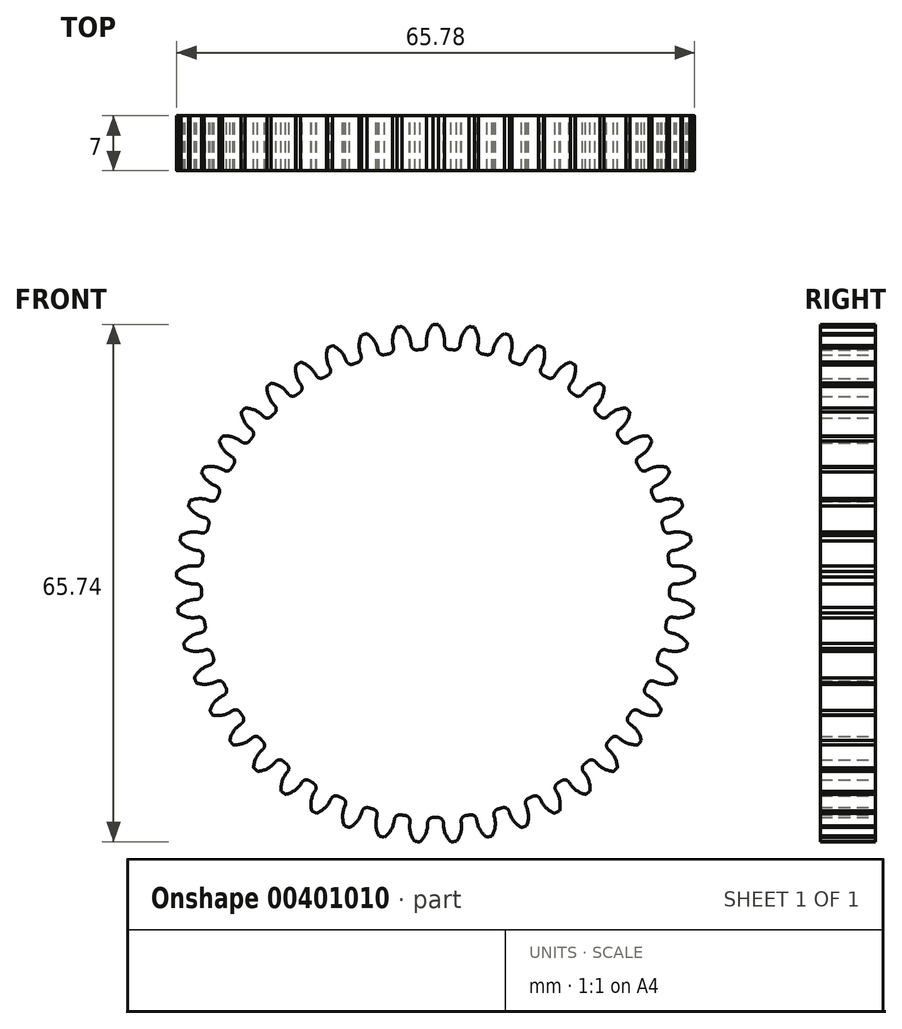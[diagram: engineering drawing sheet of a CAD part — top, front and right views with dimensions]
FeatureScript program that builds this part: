
annotation { "Feature Type Name" : "Feature", "Feature Type Description" : "" }
export const myFeature = defineFeature(function(context is Context, id is Id, definition is map)
    precondition{}
    {
        {
            var Q0;
            Q0=qCreatedBy(makeId("Front.planeOp"),FACE);
            var sketch = newSketch(context, id + "F0", { "sketchPlane" : qUnion([Q0])});
            skArc(sketch, "E0.0.0", {"start": v(-1.8, 30.22) * mm, "mid": v(-2.09, 30.2) * mm, "end": v(-2.38, 30.18) * mm});
            skArc(sketch, "E0.0.1", {"start": v(-2.38, 30.18) * mm, "mid": v(-2.9, 30.36) * mm, "end": v(-3.14, 30.85) * mm});
            skArc(sketch, "E0.0.2", {"start": v(-3.14, 30.85) * mm, "mid": v(-3.45, 32.12) * mm, "end": v(-4.25, 33.15) * mm});
            skArc(sketch, "E0.0.3", {"start": v(-4.25, 33.15) * mm, "mid": v(-4.6, 33.1) * mm, "end": v(-4.93, 33.06) * mm});
            skArc(sketch, "E0.0.4", {"start": v(-4.93, 33.06) * mm, "mid": v(-5.42, 31.84) * mm, "end": v(-5.37, 30.54) * mm});
            skArc(sketch, "E0.0.5", {"start": v(-5.37, 30.54) * mm, "mid": v(-5.46, 30) * mm, "end": v(-5.91, 29.69) * mm});
            skArc(sketch, "E0.0.6", {"start": v(-5.91, 29.69) * mm, "mid": v(-6.2, 29.63) * mm, "end": v(-6.49, 29.56) * mm});
            skArc(sketch, "E0.0.7", {"start": v(-6.49, 29.56) * mm, "mid": v(-7.03, 29.67) * mm, "end": v(-7.33, 30.12) * mm});
            skArc(sketch, "E0.0.8", {"start": v(-7.33, 30.12) * mm, "mid": v(-7.82, 31.33) * mm, "end": v(-8.75, 32.25) * mm});
            skArc(sketch, "E0.0.9", {"start": v(-8.75, 32.25) * mm, "mid": v(-9.08, 32.15) * mm, "end": v(-9.41, 32.06) * mm});
            skArc(sketch, "E0.0.10", {"start": v(-9.41, 32.06) * mm, "mid": v(-9.72, 30.79) * mm, "end": v(-9.5, 29.5) * mm});
            skArc(sketch, "E0.0.11", {"start": v(-9.5, 29.5) * mm, "mid": v(-9.5, 28.95) * mm, "end": v(-9.91, 28.58) * mm});
            skArc(sketch, "E0.0.12", {"start": v(-9.91, 28.58) * mm, "mid": v(-10.19, 28.48) * mm, "end": v(-10.46, 28.38) * mm});
            skArc(sketch, "E0.0.13", {"start": v(-10.46, 28.38) * mm, "mid": v(-11.01, 28.4) * mm, "end": v(-11.38, 28.82) * mm});
            skArc(sketch, "E0.0.14", {"start": v(-11.38, 28.82) * mm, "mid": v(-12.03, 29.95) * mm, "end": v(-13.08, 30.72) * mm});
            skArc(sketch, "E0.0.15", {"start": v(-13.08, 30.72) * mm, "mid": v(-13.4, 30.58) * mm, "end": v(-13.7, 30.44) * mm});
            skArc(sketch, "E0.0.16", {"start": v(-13.7, 30.44) * mm, "mid": v(-13.84, 29.14) * mm, "end": v(-13.44, 27.9) * mm});
            skArc(sketch, "E0.0.17", {"start": v(-13.44, 27.9) * mm, "mid": v(-13.37, 27.36) * mm, "end": v(-13.72, 26.93) * mm});
            skArc(sketch, "E0.0.18", {"start": v(-13.72, 26.93) * mm, "mid": v(-13.98, 26.8) * mm, "end": v(-14.24, 26.66) * mm});
            skArc(sketch, "E0.0.19", {"start": v(-14.24, 26.66) * mm, "mid": v(-14.79, 26.6) * mm, "end": v(-15.2, 26.96) * mm});
            skArc(sketch, "E0.0.20", {"start": v(-15.2, 26.96) * mm, "mid": v(-16, 28) * mm, "end": v(-17.15, 28.6) * mm});
            skArc(sketch, "E0.0.21", {"start": v(-17.15, 28.6) * mm, "mid": v(-17.45, 28.43) * mm, "end": v(-17.74, 28.24) * mm});
            skArc(sketch, "E0.0.22", {"start": v(-17.74, 28.24) * mm, "mid": v(-17.69, 26.94) * mm, "end": v(-17.11, 25.77) * mm});
            skArc(sketch, "E0.0.23", {"start": v(-17.11, 25.77) * mm, "mid": v(-16.97, 25.24) * mm, "end": v(-17.26, 24.77) * mm});
            skArc(sketch, "E0.0.24", {"start": v(-17.26, 24.77) * mm, "mid": v(-17.5, 24.6) * mm, "end": v(-17.74, 24.42) * mm});
            skArc(sketch, "E0.0.25", {"start": v(-17.74, 24.42) * mm, "mid": v(-18.27, 24.3) * mm, "end": v(-18.73, 24.6) * mm});
            skArc(sketch, "E0.0.26", {"start": v(-18.73, 24.6) * mm, "mid": v(-19.67, 25.5) * mm, "end": v(-20.9, 25.95) * mm});
            skArc(sketch, "E0.0.27", {"start": v(-20.9, 25.95) * mm, "mid": v(-21.16, 25.73) * mm, "end": v(-21.42, 25.5) * mm});
            skArc(sketch, "E0.0.28", {"start": v(-21.42, 25.5) * mm, "mid": v(-21.2, 24.22) * mm, "end": v(-20.46, 23.14) * mm});
            skArc(sketch, "E0.0.29", {"start": v(-20.46, 23.14) * mm, "mid": v(-20.25, 22.63) * mm, "end": v(-20.47, 22.13) * mm});
            skArc(sketch, "E0.0.30", {"start": v(-20.47, 22.13) * mm, "mid": v(-20.68, 21.93) * mm, "end": v(-20.89, 21.72) * mm});
            skArc(sketch, "E0.0.31", {"start": v(-20.89, 21.72) * mm, "mid": v(-21.4, 21.52) * mm, "end": v(-21.9, 21.75) * mm});
            skArc(sketch, "E0.0.32", {"start": v(-21.9, 21.75) * mm, "mid": v(-22.96, 22.52) * mm, "end": v(-24.23, 22.8) * mm});
            skArc(sketch, "E0.0.33", {"start": v(-24.23, 22.8) * mm, "mid": v(-24.46, 22.54) * mm, "end": v(-24.7, 22.28) * mm});
            skArc(sketch, "E0.0.34", {"start": v(-24.7, 22.28) * mm, "mid": v(-24.28, 21.05) * mm, "end": v(-23.4, 20.08) * mm});
            skArc(sketch, "E0.0.35", {"start": v(-23.4, 20.08) * mm, "mid": v(-23.13, 19.6) * mm, "end": v(-23.27, 19.07) * mm});
            skArc(sketch, "E0.0.36", {"start": v(-23.27, 19.07) * mm, "mid": v(-23.46, 18.84) * mm, "end": v(-23.64, 18.61) * mm});
            skArc(sketch, "E0.0.37", {"start": v(-23.64, 18.61) * mm, "mid": v(-24.11, 18.34) * mm, "end": v(-24.64, 18.5) * mm});
            skArc(sketch, "E0.0.38", {"start": v(-24.64, 18.5) * mm, "mid": v(-25.8, 19.11) * mm, "end": v(-27.1, 19.2) * mm});
            skArc(sketch, "E0.0.39", {"start": v(-27.1, 19.2) * mm, "mid": v(-27.29, 18.92) * mm, "end": v(-27.48, 18.64) * mm});
            skArc(sketch, "E0.0.40", {"start": v(-27.48, 18.64) * mm, "mid": v(-26.9, 17.47) * mm, "end": v(-25.9, 16.63) * mm});
            skArc(sketch, "E0.0.41", {"start": v(-25.9, 16.63) * mm, "mid": v(-25.56, 16.2) * mm, "end": v(-25.63, 15.66) * mm});
            skArc(sketch, "E0.0.42", {"start": v(-25.63, 15.66) * mm, "mid": v(-25.78, 15.4) * mm, "end": v(-25.92, 15.15) * mm});
            skArc(sketch, "E0.0.43", {"start": v(-25.92, 15.15) * mm, "mid": v(-26.36, 14.81) * mm, "end": v(-26.9, 14.9) * mm});
            skArc(sketch, "E0.0.44", {"start": v(-26.9, 14.9) * mm, "mid": v(-28.13, 15.34) * mm, "end": v(-29.43, 15.26) * mm});
            skArc(sketch, "E0.0.45", {"start": v(-29.43, 15.26) * mm, "mid": v(-29.58, 14.95) * mm, "end": v(-29.73, 14.64) * mm});
            skArc(sketch, "E0.0.46", {"start": v(-29.73, 14.64) * mm, "mid": v(-29, 13.56) * mm, "end": v(-27.9, 12.87) * mm});
            skArc(sketch, "E0.0.47", {"start": v(-27.9, 12.87) * mm, "mid": v(-27.5, 12.5) * mm, "end": v(-27.49, 11.94) * mm});
            skArc(sketch, "E0.0.48", {"start": v(-27.49, 11.94) * mm, "mid": v(-27.6, 11.67) * mm, "end": v(-27.7, 11.4) * mm});
            skArc(sketch, "E0.0.49", {"start": v(-27.7, 11.4) * mm, "mid": v(-28.1, 11) * mm, "end": v(-28.64, 11.01) * mm});
            skArc(sketch, "E0.0.50", {"start": v(-28.64, 11.01) * mm, "mid": v(-29.92, 11.29) * mm, "end": v(-31.2, 11.02) * mm});
            skArc(sketch, "E0.0.51", {"start": v(-31.2, 11.02) * mm, "mid": v(-31.3, 10.7) * mm, "end": v(-31.4, 10.37) * mm});
            skArc(sketch, "E0.0.52", {"start": v(-31.4, 10.37) * mm, "mid": v(-30.53, 9.4) * mm, "end": v(-29.34, 8.87) * mm});
            skArc(sketch, "E0.0.53", {"start": v(-29.34, 8.87) * mm, "mid": v(-28.89, 8.55) * mm, "end": v(-28.8, 8) * mm});
            skArc(sketch, "E0.0.54", {"start": v(-28.8, 8) * mm, "mid": v(-28.88, 7.72) * mm, "end": v(-28.95, 7.44) * mm});
            skArc(sketch, "E0.0.55", {"start": v(-28.95, 7.44) * mm, "mid": v(-29.28, 7) * mm, "end": v(-29.82, 6.93) * mm});
            skArc(sketch, "E0.0.56", {"start": v(-29.82, 6.93) * mm, "mid": v(-31.12, 7.02) * mm, "end": v(-32.35, 6.58) * mm});
            skArc(sketch, "E0.0.57", {"start": v(-32.35, 6.58) * mm, "mid": v(-32.41, 6.24) * mm, "end": v(-32.47, 5.9) * mm});
            skArc(sketch, "E0.0.58", {"start": v(-32.47, 5.9) * mm, "mid": v(-31.47, 5.07) * mm, "end": v(-30.21, 4.7) * mm});
            skArc(sketch, "E0.0.59", {"start": v(-30.21, 4.7) * mm, "mid": v(-29.72, 4.46) * mm, "end": v(-29.57, 3.93) * mm});
            skArc(sketch, "E0.0.60", {"start": v(-29.57, 3.93) * mm, "mid": v(-29.6, 3.64) * mm, "end": v(-29.63, 3.34) * mm});
            skArc(sketch, "E0.0.61", {"start": v(-29.63, 3.34) * mm, "mid": v(-29.9, 2.86) * mm, "end": v(-30.42, 2.72) * mm});
            skArc(sketch, "E0.0.62", {"start": v(-30.42, 2.72) * mm, "mid": v(-31.72, 2.63) * mm, "end": v(-32.88, 2.02) * mm});
            skArc(sketch, "E0.0.63", {"start": v(-32.88, 2.02) * mm, "mid": v(-32.9, 1.68) * mm, "end": v(-32.9, 1.33) * mm});
            skArc(sketch, "E0.0.64", {"start": v(-32.9, 1.33) * mm, "mid": v(-31.8, 0.65) * mm, "end": v(-30.5, 0.46) * mm});
            skArc(sketch, "E0.0.65", {"start": v(-30.5, 0.46) * mm, "mid": v(-29.98, 0.28) * mm, "end": v(-29.75, -0.22) * mm});
            skArc(sketch, "E0.0.66", {"start": v(-29.75, -0.22) * mm, "mid": v(-29.75, -0.51) * mm, "end": v(-29.73, -0.8) * mm});
            skArc(sketch, "E0.0.67", {"start": v(-29.73, -0.8) * mm, "mid": v(-29.93, -1.32) * mm, "end": v(-30.43, -1.54) * mm});
            skArc(sketch, "E0.0.68", {"start": v(-30.43, -1.54) * mm, "mid": v(-31.7, -1.8) * mm, "end": v(-32.77, -2.57) * mm});
            skArc(sketch, "E0.0.69", {"start": v(-32.77, -2.57) * mm, "mid": v(-32.73, -2.91) * mm, "end": v(-32.7, -3.25) * mm});
            skArc(sketch, "E0.0.70", {"start": v(-32.7, -3.25) * mm, "mid": v(-31.5, -3.78) * mm, "end": v(-30.2, -3.78) * mm});
            skArc(sketch, "E0.0.71", {"start": v(-30.2, -3.78) * mm, "mid": v(-29.66, -3.89) * mm, "end": v(-29.36, -4.35) * mm});
            skArc(sketch, "E0.0.72", {"start": v(-29.36, -4.35) * mm, "mid": v(-29.31, -4.64) * mm, "end": v(-29.26, -4.93) * mm});
            skArc(sketch, "E0.0.73", {"start": v(-29.26, -4.93) * mm, "mid": v(-29.38, -5.46) * mm, "end": v(-29.85, -5.75) * mm});
            skArc(sketch, "E0.0.74", {"start": v(-29.85, -5.75) * mm, "mid": v(-31.07, -6.2) * mm, "end": v(-32.02, -7.1) * mm});
            skArc(sketch, "E0.0.75", {"start": v(-32.02, -7.1) * mm, "mid": v(-31.94, -7.43) * mm, "end": v(-31.85, -7.77) * mm});
            skArc(sketch, "E0.0.76", {"start": v(-31.85, -7.77) * mm, "mid": v(-30.6, -8.12) * mm, "end": v(-29.3, -7.94) * mm});
            skArc(sketch, "E0.0.77", {"start": v(-29.3, -7.94) * mm, "mid": v(-28.75, -7.97) * mm, "end": v(-28.4, -8.39) * mm});
            skArc(sketch, "E0.0.78", {"start": v(-28.4, -8.39) * mm, "mid": v(-28.3, -8.67) * mm, "end": v(-28.22, -8.95) * mm});
            skArc(sketch, "E0.0.79", {"start": v(-28.22, -8.95) * mm, "mid": v(-28.26, -9.5) * mm, "end": v(-28.68, -9.84) * mm});
            skArc(sketch, "E0.0.80", {"start": v(-28.68, -9.84) * mm, "mid": v(-29.84, -10.45) * mm, "end": v(-30.65, -11.48) * mm});
            skArc(sketch, "E0.0.81", {"start": v(-30.65, -11.48) * mm, "mid": v(-30.52, -11.8) * mm, "end": v(-30.39, -12.12) * mm});
            skArc(sketch, "E0.0.82", {"start": v(-30.39, -12.12) * mm, "mid": v(-29.1, -12.3) * mm, "end": v(-27.84, -11.93) * mm});
            skArc(sketch, "E0.0.83", {"start": v(-27.84, -11.93) * mm, "mid": v(-27.3, -11.89) * mm, "end": v(-26.88, -12.25) * mm});
            skArc(sketch, "E0.0.84", {"start": v(-26.88, -12.25) * mm, "mid": v(-26.75, -12.51) * mm, "end": v(-26.62, -12.78) * mm});
            skArc(sketch, "E0.0.85", {"start": v(-26.62, -12.78) * mm, "mid": v(-26.59, -13.33) * mm, "end": v(-26.96, -13.73) * mm});
            skArc(sketch, "E0.0.86", {"start": v(-26.96, -13.73) * mm, "mid": v(-28.02, -14.5) * mm, "end": v(-28.68, -15.62) * mm});
            skArc(sketch, "E0.0.87", {"start": v(-28.68, -15.62) * mm, "mid": v(-28.5, -15.92) * mm, "end": v(-28.33, -16.22) * mm});
            skArc(sketch, "E0.0.88", {"start": v(-28.33, -16.22) * mm, "mid": v(-27.03, -16.21) * mm, "end": v(-25.83, -15.68) * mm});
            skArc(sketch, "E0.0.89", {"start": v(-25.83, -15.68) * mm, "mid": v(-25.3, -15.56) * mm, "end": v(-24.84, -15.86) * mm});
            skArc(sketch, "E0.0.90", {"start": v(-24.84, -15.86) * mm, "mid": v(-24.68, -16.1) * mm, "end": v(-24.51, -16.35) * mm});
            skArc(sketch, "E0.0.91", {"start": v(-24.51, -16.35) * mm, "mid": v(-24.4, -16.9) * mm, "end": v(-24.72, -17.34) * mm});
            skArc(sketch, "E0.0.92", {"start": v(-24.72, -17.34) * mm, "mid": v(-25.65, -18.25) * mm, "end": v(-26.15, -19.46) * mm});
            skArc(sketch, "E0.0.93", {"start": v(-26.15, -19.46) * mm, "mid": v(-25.94, -19.73) * mm, "end": v(-25.73, -20) * mm});
            skArc(sketch, "E0.0.94", {"start": v(-25.73, -20) * mm, "mid": v(-24.43, -19.81) * mm, "end": v(-23.33, -19.12) * mm});
            skArc(sketch, "E0.0.95", {"start": v(-23.33, -19.12) * mm, "mid": v(-22.81, -18.92) * mm, "end": v(-22.32, -19.16) * mm});
            skArc(sketch, "E0.0.96", {"start": v(-22.32, -19.16) * mm, "mid": v(-22.12, -19.38) * mm, "end": v(-21.92, -19.6) * mm});
            skArc(sketch, "E0.0.97", {"start": v(-21.92, -19.6) * mm, "mid": v(-21.74, -20.12) * mm, "end": v(-21.99, -20.6) * mm});
            skArc(sketch, "E0.0.98", {"start": v(-21.99, -20.6) * mm, "mid": v(-22.8, -21.63) * mm, "end": v(-23.11, -22.9) * mm});
            skArc(sketch, "E0.0.99", {"start": v(-23.11, -22.9) * mm, "mid": v(-22.87, -23.14) * mm, "end": v(-22.62, -23.38) * mm});
            skArc(sketch, "E0.0.100", {"start": v(-22.62, -23.38) * mm, "mid": v(-21.37, -23.01) * mm, "end": v(-20.37, -22.17) * mm});
            skArc(sketch, "E0.0.101", {"start": v(-20.37, -22.17) * mm, "mid": v(-19.88, -21.9) * mm, "end": v(-19.36, -22.07) * mm});
            skArc(sketch, "E0.0.102", {"start": v(-19.36, -22.07) * mm, "mid": v(-19.14, -22.26) * mm, "end": v(-18.91, -22.45) * mm});
            skArc(sketch, "E0.0.103", {"start": v(-18.91, -22.45) * mm, "mid": v(-18.66, -22.94) * mm, "end": v(-18.83, -23.46) * mm});
            skArc(sketch, "E0.0.104", {"start": v(-18.83, -23.46) * mm, "mid": v(-19.49, -24.59) * mm, "end": v(-19.63, -25.89) * mm});
            skArc(sketch, "E0.0.105", {"start": v(-19.63, -25.89) * mm, "mid": v(-19.35, -26.09) * mm, "end": v(-19.07, -26.3) * mm});
            skArc(sketch, "E0.0.106", {"start": v(-19.07, -26.3) * mm, "mid": v(-17.88, -25.75) * mm, "end": v(-17, -24.78) * mm});
            skArc(sketch, "E0.0.107", {"start": v(-17, -24.78) * mm, "mid": v(-16.57, -24.45) * mm, "end": v(-16.03, -24.55) * mm});
            skArc(sketch, "E0.0.108", {"start": v(-16.03, -24.55) * mm, "mid": v(-15.78, -24.7) * mm, "end": v(-15.53, -24.86) * mm});
            skArc(sketch, "E0.0.109", {"start": v(-15.53, -24.86) * mm, "mid": v(-15.2, -25.3) * mm, "end": v(-15.31, -25.84) * mm});
            skArc(sketch, "E0.0.110", {"start": v(-15.31, -25.84) * mm, "mid": v(-15.8, -27.05) * mm, "end": v(-15.76, -28.36) * mm});
            skArc(sketch, "E0.0.111", {"start": v(-15.76, -28.36) * mm, "mid": v(-15.46, -28.52) * mm, "end": v(-15.15, -28.68) * mm});
            skArc(sketch, "E0.0.112", {"start": v(-15.15, -28.68) * mm, "mid": v(-14.05, -27.98) * mm, "end": v(-13.32, -26.9) * mm});
            skArc(sketch, "E0.0.113", {"start": v(-13.32, -26.9) * mm, "mid": v(-12.93, -26.52) * mm, "end": v(-12.38, -26.53) * mm});
            skArc(sketch, "E0.0.114", {"start": v(-12.38, -26.53) * mm, "mid": v(-12.11, -26.65) * mm, "end": v(-11.84, -26.77) * mm});
            skArc(sketch, "E0.0.115", {"start": v(-11.84, -26.77) * mm, "mid": v(-11.47, -27.17) * mm, "end": v(-11.5, -27.72) * mm});
            skArc(sketch, "E0.0.116", {"start": v(-11.5, -27.72) * mm, "mid": v(-11.8, -28.98) * mm, "end": v(-11.59, -30.27) * mm});
            skArc(sketch, "E0.0.117", {"start": v(-11.59, -30.27) * mm, "mid": v(-11.27, -30.39) * mm, "end": v(-10.94, -30.5) * mm});
            skArc(sketch, "E0.0.118", {"start": v(-10.94, -30.5) * mm, "mid": v(-9.95, -29.66) * mm, "end": v(-9.37, -28.49) * mm});
            skArc(sketch, "E0.0.119", {"start": v(-9.37, -28.49) * mm, "mid": v(-9.04, -28.05) * mm, "end": v(-8.5, -27.99) * mm});
            skArc(sketch, "E0.0.120", {"start": v(-8.5, -27.99) * mm, "mid": v(-8.21, -28.07) * mm, "end": v(-7.93, -28.15) * mm});
            skArc(sketch, "E0.0.121", {"start": v(-7.93, -28.15) * mm, "mid": v(-7.5, -28.5) * mm, "end": v(-7.45, -29.04) * mm});
            skArc(sketch, "E0.0.122", {"start": v(-7.45, -29.04) * mm, "mid": v(-7.59, -30.34) * mm, "end": v(-7.2, -31.58) * mm});
            skArc(sketch, "E0.0.123", {"start": v(-7.2, -31.58) * mm, "mid": v(-6.85, -31.65) * mm, "end": v(-6.52, -31.72) * mm});
            skArc(sketch, "E0.0.124", {"start": v(-6.52, -31.72) * mm, "mid": v(-5.65, -30.75) * mm, "end": v(-5.24, -29.5) * mm});
            skArc(sketch, "E0.0.125", {"start": v(-5.24, -29.5) * mm, "mid": v(-4.98, -29.03) * mm, "end": v(-4.44, -28.9) * mm});
            skArc(sketch, "E0.0.126", {"start": v(-4.44, -28.9) * mm, "mid": v(-4.15, -28.93) * mm, "end": v(-3.86, -28.97) * mm});
            skArc(sketch, "E0.0.127", {"start": v(-3.86, -28.97) * mm, "mid": v(-3.39, -29.25) * mm, "end": v(-3.26, -29.79) * mm});
            skArc(sketch, "E0.0.128", {"start": v(-3.26, -29.79) * mm, "mid": v(-3.22, -31.1) * mm, "end": v(-2.65, -32.27) * mm});
            skArc(sketch, "E0.0.129", {"start": v(-2.65, -32.27) * mm, "mid": v(-2.3, -32.3) * mm, "end": v(-1.96, -32.31) * mm});
            skArc(sketch, "E0.0.130", {"start": v(-1.96, -32.31) * mm, "mid": v(-1.24, -31.23) * mm, "end": v(-1.01, -29.94) * mm});
            skArc(sketch, "E0.0.131", {"start": v(-1.01, -29.94) * mm, "mid": v(-0.81, -29.43) * mm, "end": v(-0.3, -29.22) * mm});
            skArc(sketch, "E0.0.132", {"start": v(-0.3, -29.22) * mm, "mid": v(-0.01, -29.22) * mm, "end": v(0.28, -29.22) * mm});
            skArc(sketch, "E0.0.133", {"start": v(0.28, -29.22) * mm, "mid": v(0.79, -29.43) * mm, "end": v(0.99, -29.94) * mm});
            skArc(sketch, "E0.0.134", {"start": v(0.99, -29.94) * mm, "mid": v(1.21, -31.23) * mm, "end": v(1.94, -32.31) * mm});
            skArc(sketch, "E0.0.135", {"start": v(1.94, -32.31) * mm, "mid": v(2.28, -32.3) * mm, "end": v(2.63, -32.27) * mm});
            skArc(sketch, "E0.0.136", {"start": v(2.63, -32.27) * mm, "mid": v(3.2, -31.1) * mm, "end": v(3.24, -29.79) * mm});
            skArc(sketch, "E0.0.137", {"start": v(3.24, -29.79) * mm, "mid": v(3.36, -29.25) * mm, "end": v(3.84, -28.97) * mm});
            skArc(sketch, "E0.0.138", {"start": v(3.84, -28.97) * mm, "mid": v(4.13, -28.93) * mm, "end": v(4.42, -28.9) * mm});
            skArc(sketch, "E0.0.139", {"start": v(4.42, -28.9) * mm, "mid": v(4.95, -29.03) * mm, "end": v(5.22, -29.5) * mm});
            skArc(sketch, "E0.0.140", {"start": v(5.22, -29.5) * mm, "mid": v(5.62, -30.75) * mm, "end": v(6.49, -31.72) * mm});
            skArc(sketch, "E0.0.141", {"start": v(6.49, -31.72) * mm, "mid": v(6.83, -31.65) * mm, "end": v(7.16, -31.58) * mm});
            skArc(sketch, "E0.0.142", {"start": v(7.16, -31.58) * mm, "mid": v(7.56, -30.34) * mm, "end": v(7.42, -29.04) * mm});
            skArc(sketch, "E0.0.143", {"start": v(7.42, -29.04) * mm, "mid": v(7.47, -28.5) * mm, "end": v(7.9, -28.15) * mm});
            skArc(sketch, "E0.0.144", {"start": v(7.9, -28.15) * mm, "mid": v(8.19, -28.07) * mm, "end": v(8.47, -27.99) * mm});
            skArc(sketch, "E0.0.145", {"start": v(8.47, -27.99) * mm, "mid": v(9.01, -28.05) * mm, "end": v(9.35, -28.49) * mm});
            skArc(sketch, "E0.0.146", {"start": v(9.35, -28.49) * mm, "mid": v(9.92, -29.66) * mm, "end": v(10.91, -30.5) * mm});
            skArc(sketch, "E0.0.147", {"start": v(10.91, -30.5) * mm, "mid": v(11.24, -30.39) * mm, "end": v(11.56, -30.27) * mm});
            skArc(sketch, "E0.0.148", {"start": v(11.56, -30.27) * mm, "mid": v(11.78, -28.98) * mm, "end": v(11.47, -27.72) * mm});
            skArc(sketch, "E0.0.149", {"start": v(11.47, -27.72) * mm, "mid": v(11.44, -27.17) * mm, "end": v(11.82, -26.77) * mm});
            skArc(sketch, "E0.0.150", {"start": v(11.82, -26.77) * mm, "mid": v(12.09, -26.65) * mm, "end": v(12.36, -26.53) * mm});
            skArc(sketch, "E0.0.151", {"start": v(12.36, -26.53) * mm, "mid": v(12.9, -26.52) * mm, "end": v(13.3, -26.9) * mm});
            skArc(sketch, "E0.0.152", {"start": v(13.3, -26.9) * mm, "mid": v(14.02, -27.98) * mm, "end": v(15.13, -28.68) * mm});
            skArc(sketch, "E0.0.153", {"start": v(15.13, -28.68) * mm, "mid": v(15.43, -28.52) * mm, "end": v(15.74, -28.36) * mm});
            skArc(sketch, "E0.0.154", {"start": v(15.74, -28.36) * mm, "mid": v(15.77, -27.05) * mm, "end": v(15.29, -25.84) * mm});
            skArc(sketch, "E0.0.155", {"start": v(15.29, -25.84) * mm, "mid": v(15.18, -25.3) * mm, "end": v(15.5, -24.86) * mm});
            skArc(sketch, "E0.0.156", {"start": v(15.5, -24.86) * mm, "mid": v(15.75, -24.7) * mm, "end": v(16, -24.55) * mm});
            skArc(sketch, "E0.0.157", {"start": v(16, -24.55) * mm, "mid": v(16.54, -24.45) * mm, "end": v(16.98, -24.78) * mm});
            skArc(sketch, "E0.0.158", {"start": v(16.98, -24.78) * mm, "mid": v(17.86, -25.75) * mm, "end": v(19.04, -26.3) * mm});
            skArc(sketch, "E0.0.159", {"start": v(19.04, -26.3) * mm, "mid": v(19.32, -26.09) * mm, "end": v(19.6, -25.89) * mm});
            skArc(sketch, "E0.0.160", {"start": v(19.6, -25.89) * mm, "mid": v(19.46, -24.59) * mm, "end": v(18.8, -23.46) * mm});
            skArc(sketch, "E0.0.161", {"start": v(18.8, -23.46) * mm, "mid": v(18.63, -22.94) * mm, "end": v(18.88, -22.45) * mm});
            skArc(sketch, "E0.0.162", {"start": v(18.88, -22.45) * mm, "mid": v(19.1, -22.26) * mm, "end": v(19.33, -22.07) * mm});
            skArc(sketch, "E0.0.163", {"start": v(19.33, -22.07) * mm, "mid": v(19.86, -21.9) * mm, "end": v(20.34, -22.17) * mm});
            skArc(sketch, "E0.0.164", {"start": v(20.34, -22.17) * mm, "mid": v(21.34, -23.01) * mm, "end": v(22.6, -23.38) * mm});
            skArc(sketch, "E0.0.165", {"start": v(22.6, -23.38) * mm, "mid": v(22.84, -23.14) * mm, "end": v(23.09, -22.9) * mm});
            skArc(sketch, "E0.0.166", {"start": v(23.09, -22.9) * mm, "mid": v(22.77, -21.63) * mm, "end": v(21.96, -20.6) * mm});
            skArc(sketch, "E0.0.167", {"start": v(21.96, -20.6) * mm, "mid": v(21.71, -20.12) * mm, "end": v(21.9, -19.6) * mm});
            skArc(sketch, "E0.0.168", {"start": v(21.9, -19.6) * mm, "mid": v(22.1, -19.38) * mm, "end": v(22.3, -19.16) * mm});
            skArc(sketch, "E0.0.169", {"start": v(22.3, -19.16) * mm, "mid": v(22.79, -18.92) * mm, "end": v(23.3, -19.12) * mm});
            skArc(sketch, "E0.0.170", {"start": v(23.3, -19.12) * mm, "mid": v(24.4, -19.81) * mm, "end": v(25.7, -20) * mm});
            skArc(sketch, "E0.0.171", {"start": v(25.7, -20) * mm, "mid": v(25.91, -19.73) * mm, "end": v(26.12, -19.46) * mm});
            skArc(sketch, "E0.0.172", {"start": v(26.12, -19.46) * mm, "mid": v(25.63, -18.25) * mm, "end": v(24.69, -17.34) * mm});
            skArc(sketch, "E0.0.173", {"start": v(24.69, -17.34) * mm, "mid": v(24.38, -16.9) * mm, "end": v(24.48, -16.35) * mm});
            skArc(sketch, "E0.0.174", {"start": v(24.48, -16.35) * mm, "mid": v(24.65, -16.1) * mm, "end": v(24.81, -15.86) * mm});
            skArc(sketch, "E0.0.175", {"start": v(24.81, -15.86) * mm, "mid": v(25.27, -15.56) * mm, "end": v(25.8, -15.68) * mm});
            skArc(sketch, "E0.0.176", {"start": v(25.8, -15.68) * mm, "mid": v(27, -16.21) * mm, "end": v(28.3, -16.22) * mm});
            skArc(sketch, "E0.0.177", {"start": v(28.3, -16.22) * mm, "mid": v(28.48, -15.92) * mm, "end": v(28.65, -15.62) * mm});
            skArc(sketch, "E0.0.178", {"start": v(28.65, -15.62) * mm, "mid": v(28, -14.5) * mm, "end": v(26.94, -13.73) * mm});
            skArc(sketch, "E0.0.179", {"start": v(26.94, -13.73) * mm, "mid": v(26.56, -13.33) * mm, "end": v(26.6, -12.78) * mm});
            skArc(sketch, "E0.0.180", {"start": v(26.6, -12.78) * mm, "mid": v(26.73, -12.51) * mm, "end": v(26.85, -12.25) * mm});
            skArc(sketch, "E0.0.181", {"start": v(26.85, -12.25) * mm, "mid": v(27.27, -11.89) * mm, "end": v(27.81, -11.93) * mm});
            skArc(sketch, "E0.0.182", {"start": v(27.81, -11.93) * mm, "mid": v(29.07, -12.3) * mm, "end": v(30.36, -12.12) * mm});
            skArc(sketch, "E0.0.183", {"start": v(30.36, -12.12) * mm, "mid": v(30.5, -11.8) * mm, "end": v(30.62, -11.48) * mm});
            skArc(sketch, "E0.0.184", {"start": v(30.62, -11.48) * mm, "mid": v(29.8, -10.45) * mm, "end": v(28.66, -9.84) * mm});
            skArc(sketch, "E0.0.185", {"start": v(28.66, -9.84) * mm, "mid": v(28.23, -9.5) * mm, "end": v(28.19, -8.95) * mm});
            skArc(sketch, "E0.0.186", {"start": v(28.19, -8.95) * mm, "mid": v(28.28, -8.67) * mm, "end": v(28.37, -8.39) * mm});
            skArc(sketch, "E0.0.187", {"start": v(28.37, -8.39) * mm, "mid": v(28.73, -7.97) * mm, "end": v(29.28, -7.94) * mm});
            skArc(sketch, "E0.0.188", {"start": v(29.28, -7.94) * mm, "mid": v(30.57, -8.12) * mm, "end": v(31.82, -7.77) * mm});
            skArc(sketch, "E0.0.189", {"start": v(31.82, -7.77) * mm, "mid": v(31.9, -7.43) * mm, "end": v(32, -7.1) * mm});
            skArc(sketch, "E0.0.190", {"start": v(32, -7.1) * mm, "mid": v(31.05, -6.2) * mm, "end": v(29.82, -5.75) * mm});
            skArc(sketch, "E0.0.191", {"start": v(29.82, -5.75) * mm, "mid": v(29.35, -5.46) * mm, "end": v(29.23, -4.93) * mm});
            skArc(sketch, "E0.0.192", {"start": v(29.23, -4.93) * mm, "mid": v(29.28, -4.64) * mm, "end": v(29.33, -4.35) * mm});
            skArc(sketch, "E0.0.193", {"start": v(29.33, -4.35) * mm, "mid": v(29.63, -3.89) * mm, "end": v(30.17, -3.78) * mm});
            skArc(sketch, "E0.0.194", {"start": v(30.17, -3.78) * mm, "mid": v(31.47, -3.78) * mm, "end": v(32.67, -3.25) * mm});
            skArc(sketch, "E0.0.195", {"start": v(32.67, -3.25) * mm, "mid": v(32.7, -2.91) * mm, "end": v(32.74, -2.57) * mm});
            skArc(sketch, "E0.0.196", {"start": v(32.74, -2.57) * mm, "mid": v(31.68, -1.8) * mm, "end": v(30.4, -1.54) * mm});
            skArc(sketch, "E0.0.197", {"start": v(30.4, -1.54) * mm, "mid": v(29.9, -1.32) * mm, "end": v(29.7, -0.8) * mm});
            skArc(sketch, "E0.0.198", {"start": v(29.7, -0.8) * mm, "mid": v(29.72, -0.51) * mm, "end": v(29.73, -0.22) * mm});
            skArc(sketch, "E0.0.199", {"start": v(29.73, -0.22) * mm, "mid": v(29.96, 0.28) * mm, "end": v(30.47, 0.46) * mm});
            skArc(sketch, "E0.0.200", {"start": v(30.47, 0.46) * mm, "mid": v(31.77, 0.65) * mm, "end": v(32.88, 1.33) * mm});
            skArc(sketch, "E0.0.201", {"start": v(32.88, 1.33) * mm, "mid": v(32.87, 1.68) * mm, "end": v(32.85, 2.02) * mm});
            skArc(sketch, "E0.0.202", {"start": v(32.85, 2.02) * mm, "mid": v(31.7, 2.63) * mm, "end": v(30.4, 2.72) * mm});
            skArc(sketch, "E0.0.203", {"start": v(30.4, 2.72) * mm, "mid": v(29.87, 2.86) * mm, "end": v(29.6, 3.34) * mm});
            skArc(sketch, "E0.0.204", {"start": v(29.6, 3.34) * mm, "mid": v(29.57, 3.64) * mm, "end": v(29.54, 3.93) * mm});
            skArc(sketch, "E0.0.205", {"start": v(29.54, 3.93) * mm, "mid": v(29.7, 4.46) * mm, "end": v(30.19, 4.7) * mm});
            skArc(sketch, "E0.0.206", {"start": v(30.19, 4.7) * mm, "mid": v(31.44, 5.07) * mm, "end": v(32.44, 5.9) * mm});
            skArc(sketch, "E0.0.207", {"start": v(32.44, 5.9) * mm, "mid": v(32.39, 6.24) * mm, "end": v(32.33, 6.58) * mm});
            skArc(sketch, "E0.0.208", {"start": v(32.33, 6.58) * mm, "mid": v(31.1, 7.02) * mm, "end": v(29.8, 6.93) * mm});
            skArc(sketch, "E0.0.209", {"start": v(29.8, 6.93) * mm, "mid": v(29.25, 7) * mm, "end": v(28.92, 7.44) * mm});
            skArc(sketch, "E0.0.210", {"start": v(28.92, 7.44) * mm, "mid": v(28.85, 7.72) * mm, "end": v(28.78, 8) * mm});
            skArc(sketch, "E0.0.211", {"start": v(28.78, 8) * mm, "mid": v(28.86, 8.55) * mm, "end": v(29.31, 8.87) * mm});
            skArc(sketch, "E0.0.212", {"start": v(29.31, 8.87) * mm, "mid": v(30.5, 9.4) * mm, "end": v(31.38, 10.37) * mm});
            skArc(sketch, "E0.0.213", {"start": v(31.38, 10.37) * mm, "mid": v(31.28, 10.7) * mm, "end": v(31.17, 11.02) * mm});
            skArc(sketch, "E0.0.214", {"start": v(31.17, 11.02) * mm, "mid": v(29.9, 11.29) * mm, "end": v(28.61, 11.01) * mm});
            skArc(sketch, "E0.0.215", {"start": v(28.61, 11.01) * mm, "mid": v(28.06, 11) * mm, "end": v(27.68, 11.4) * mm});
            skArc(sketch, "E0.0.216", {"start": v(27.68, 11.4) * mm, "mid": v(27.57, 11.67) * mm, "end": v(27.46, 11.94) * mm});
            skArc(sketch, "E0.0.217", {"start": v(27.46, 11.94) * mm, "mid": v(27.46, 12.5) * mm, "end": v(27.86, 12.87) * mm});
            skArc(sketch, "E0.0.218", {"start": v(27.86, 12.87) * mm, "mid": v(28.97, 13.56) * mm, "end": v(29.7, 14.64) * mm});
            skArc(sketch, "E0.0.219", {"start": v(29.7, 14.64) * mm, "mid": v(29.56, 14.95) * mm, "end": v(29.4, 15.26) * mm});
            skArc(sketch, "E0.0.220", {"start": v(29.4, 15.26) * mm, "mid": v(28.1, 15.34) * mm, "end": v(26.88, 14.9) * mm});
            skArc(sketch, "E0.0.221", {"start": v(26.88, 14.9) * mm, "mid": v(26.33, 14.81) * mm, "end": v(25.9, 15.15) * mm});
            skArc(sketch, "E0.0.222", {"start": v(25.9, 15.15) * mm, "mid": v(25.75, 15.4) * mm, "end": v(25.6, 15.66) * mm});
            skArc(sketch, "E0.0.223", {"start": v(25.6, 15.66) * mm, "mid": v(25.53, 16.2) * mm, "end": v(25.88, 16.63) * mm});
            skArc(sketch, "E0.0.224", {"start": v(25.88, 16.63) * mm, "mid": v(26.88, 17.47) * mm, "end": v(27.45, 18.64) * mm});
            skArc(sketch, "E0.0.225", {"start": v(27.45, 18.64) * mm, "mid": v(27.26, 18.92) * mm, "end": v(27.07, 19.2) * mm});
            skArc(sketch, "E0.0.226", {"start": v(27.07, 19.2) * mm, "mid": v(25.77, 19.11) * mm, "end": v(24.61, 18.5) * mm});
            skArc(sketch, "E0.0.227", {"start": v(24.61, 18.5) * mm, "mid": v(24.09, 18.34) * mm, "end": v(23.6, 18.61) * mm});
            skArc(sketch, "E0.0.228", {"start": v(23.6, 18.61) * mm, "mid": v(23.43, 18.84) * mm, "end": v(23.25, 19.07) * mm});
            skArc(sketch, "E0.0.229", {"start": v(23.25, 19.07) * mm, "mid": v(23.1, 19.6) * mm, "end": v(23.38, 20.08) * mm});
            skArc(sketch, "E0.0.230", {"start": v(23.38, 20.08) * mm, "mid": v(24.26, 21.05) * mm, "end": v(24.67, 22.28) * mm});
            skArc(sketch, "E0.0.231", {"start": v(24.67, 22.28) * mm, "mid": v(24.44, 22.54) * mm, "end": v(24.2, 22.8) * mm});
            skArc(sketch, "E0.0.232", {"start": v(24.2, 22.8) * mm, "mid": v(22.93, 22.52) * mm, "end": v(21.87, 21.75) * mm});
            skArc(sketch, "E0.0.233", {"start": v(21.87, 21.75) * mm, "mid": v(21.37, 21.52) * mm, "end": v(20.86, 21.72) * mm});
            skArc(sketch, "E0.0.234", {"start": v(20.86, 21.72) * mm, "mid": v(20.65, 21.93) * mm, "end": v(20.44, 22.13) * mm});
            skArc(sketch, "E0.0.235", {"start": v(20.44, 22.13) * mm, "mid": v(20.22, 22.63) * mm, "end": v(20.43, 23.14) * mm});
            skArc(sketch, "E0.0.236", {"start": v(20.43, 23.14) * mm, "mid": v(21.16, 24.22) * mm, "end": v(21.4, 25.5) * mm});
            skArc(sketch, "E0.0.237", {"start": v(21.4, 25.5) * mm, "mid": v(21.13, 25.73) * mm, "end": v(20.87, 25.95) * mm});
            skArc(sketch, "E0.0.238", {"start": v(20.87, 25.95) * mm, "mid": v(19.65, 25.5) * mm, "end": v(18.7, 24.6) * mm});
            skArc(sketch, "E0.0.239", {"start": v(18.7, 24.6) * mm, "mid": v(18.24, 24.3) * mm, "end": v(17.71, 24.42) * mm});
            skArc(sketch, "E0.0.240", {"start": v(17.71, 24.42) * mm, "mid": v(17.47, 24.6) * mm, "end": v(17.23, 24.77) * mm});
            skArc(sketch, "E0.0.241", {"start": v(17.23, 24.77) * mm, "mid": v(16.95, 25.24) * mm, "end": v(17.09, 25.77) * mm});
            skArc(sketch, "E0.0.242", {"start": v(17.09, 25.77) * mm, "mid": v(17.66, 26.94) * mm, "end": v(17.71, 28.24) * mm});
            skArc(sketch, "E0.0.243", {"start": v(17.71, 28.24) * mm, "mid": v(17.42, 28.43) * mm, "end": v(17.13, 28.6) * mm});
            skArc(sketch, "E0.0.244", {"start": v(17.13, 28.6) * mm, "mid": v(15.98, 28) * mm, "end": v(15.18, 26.96) * mm});
            skArc(sketch, "E0.0.245", {"start": v(15.18, 26.96) * mm, "mid": v(14.76, 26.6) * mm, "end": v(14.21, 26.66) * mm});
            skArc(sketch, "E0.0.246", {"start": v(14.21, 26.66) * mm, "mid": v(13.95, 26.8) * mm, "end": v(13.7, 26.93) * mm});
            skArc(sketch, "E0.0.247", {"start": v(13.7, 26.93) * mm, "mid": v(13.34, 27.36) * mm, "end": v(13.4, 27.9) * mm});
            skArc(sketch, "E0.0.248", {"start": v(13.4, 27.9) * mm, "mid": v(13.81, 29.14) * mm, "end": v(13.68, 30.44) * mm});
            skArc(sketch, "E0.0.249", {"start": v(13.68, 30.44) * mm, "mid": v(13.37, 30.58) * mm, "end": v(13.05, 30.72) * mm});
            skArc(sketch, "E0.0.250", {"start": v(13.05, 30.72) * mm, "mid": v(12, 29.95) * mm, "end": v(11.35, 28.82) * mm});
            skArc(sketch, "E0.0.251", {"start": v(11.35, 28.82) * mm, "mid": v(10.99, 28.4) * mm, "end": v(10.44, 28.38) * mm});
            skArc(sketch, "E0.0.252", {"start": v(10.44, 28.38) * mm, "mid": v(10.16, 28.48) * mm, "end": v(9.88, 28.58) * mm});
            skArc(sketch, "E0.0.253", {"start": v(9.88, 28.58) * mm, "mid": v(9.48, 28.95) * mm, "end": v(9.47, 29.5) * mm});
            skArc(sketch, "E0.0.254", {"start": v(9.47, 29.5) * mm, "mid": v(9.7, 30.79) * mm, "end": v(9.39, 32.06) * mm});
            skArc(sketch, "E0.0.255", {"start": v(9.39, 32.06) * mm, "mid": v(9.06, 32.15) * mm, "end": v(8.72, 32.25) * mm});
            skArc(sketch, "E0.0.256", {"start": v(8.72, 32.25) * mm, "mid": v(7.79, 31.33) * mm, "end": v(7.3, 30.12) * mm});
            skArc(sketch, "E0.0.257", {"start": v(7.3, 30.12) * mm, "mid": v(7, 29.67) * mm, "end": v(6.46, 29.56) * mm});
            skArc(sketch, "E0.0.258", {"start": v(6.46, 29.56) * mm, "mid": v(6.17, 29.63) * mm, "end": v(5.88, 29.69) * mm});
            skArc(sketch, "E0.0.259", {"start": v(5.88, 29.69) * mm, "mid": v(5.43, 30) * mm, "end": v(5.34, 30.54) * mm});
            skArc(sketch, "E0.0.260", {"start": v(5.34, 30.54) * mm, "mid": v(5.39, 31.84) * mm, "end": v(4.9, 33.06) * mm});
            skArc(sketch, "E0.0.261", {"start": v(4.9, 33.06) * mm, "mid": v(4.57, 33.1) * mm, "end": v(4.22, 33.15) * mm});
            skArc(sketch, "E0.0.262", {"start": v(4.22, 33.15) * mm, "mid": v(3.43, 32.12) * mm, "end": v(3.11, 30.85) * mm});
            skArc(sketch, "E0.0.263", {"start": v(3.11, 30.85) * mm, "mid": v(2.88, 30.36) * mm, "end": v(2.36, 30.18) * mm});
            skArc(sketch, "E0.0.264", {"start": v(2.36, 30.18) * mm, "mid": v(2.06, 30.2) * mm, "end": v(1.77, 30.22) * mm});
            skArc(sketch, "E0.0.265", {"start": v(1.77, 30.22) * mm, "mid": v(1.28, 30.47) * mm, "end": v(1.11, 31) * mm});
            skArc(sketch, "E0.0.266", {"start": v(1.11, 31) * mm, "mid": v(0.98, 32.3) * mm, "end": v(0.33, 33.43) * mm});
            skArc(sketch, "E0.0.267", {"start": v(0.33, 33.43) * mm, "mid": v(-0.01, 33.43) * mm, "end": v(-0.36, 33.43) * mm});
            skArc(sketch, "E0.0.268", {"start": v(-0.36, 33.43) * mm, "mid": v(-1, 32.3) * mm, "end": v(-1.14, 31) * mm});
            skArc(sketch, "E0.0.269", {"start": v(-1.14, 31) * mm, "mid": v(-1.3, 30.47) * mm, "end": v(-1.8, 30.22) * mm});
            skSolve(sketch);
        }
        {
            var Q0;
            Q0 = qSketchRegion(id + "F0", true);
            extrude(context, id + "F1", {"entities" : qUnion([Q0]), "depth" : 7 * mm});
        }
    });
